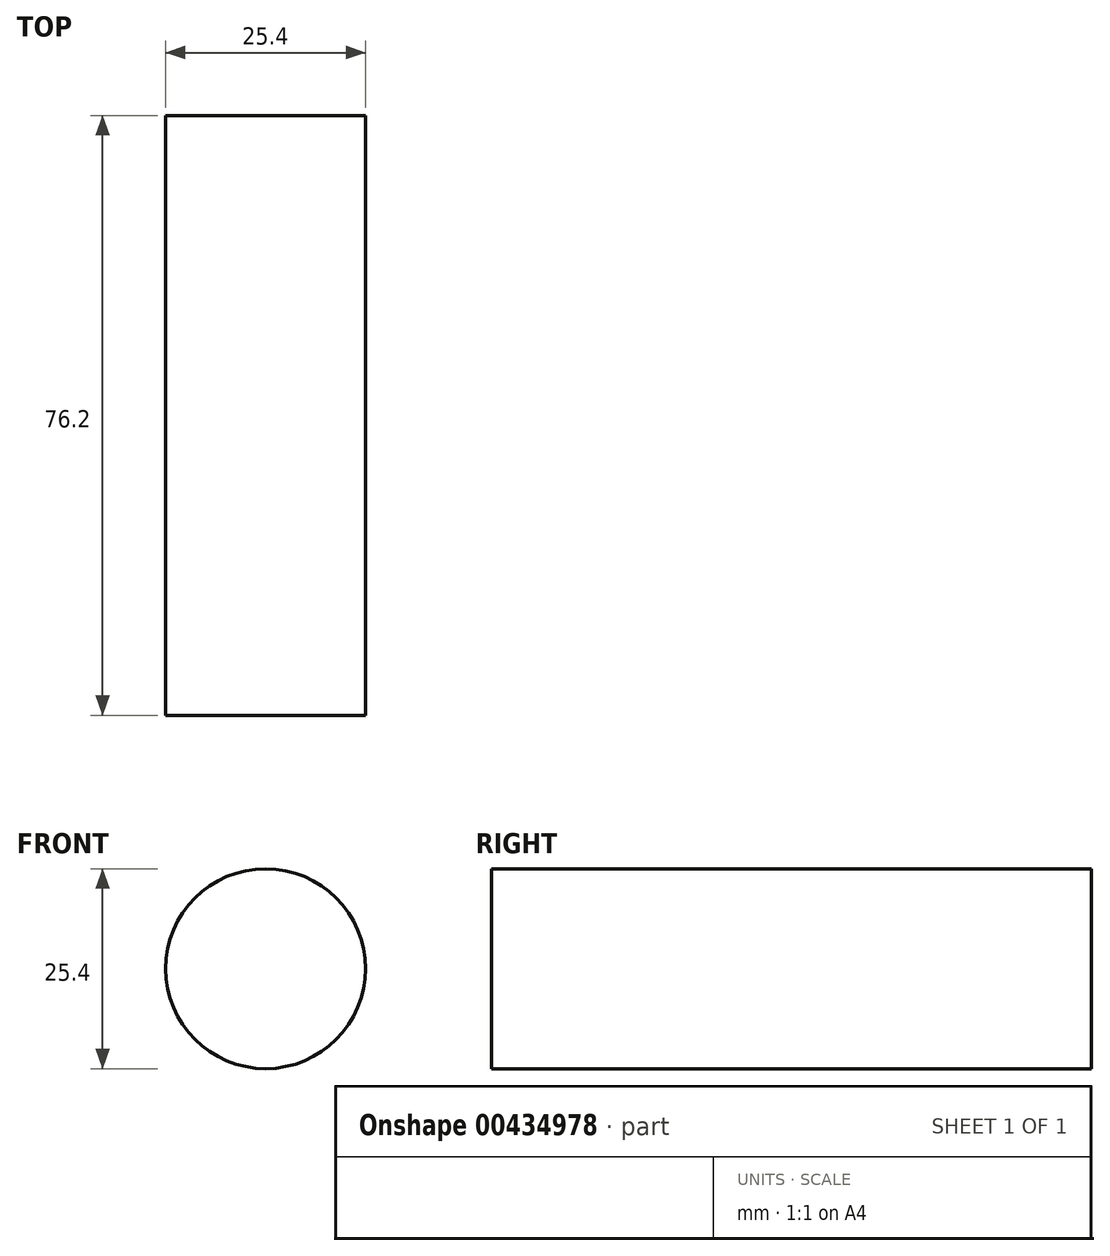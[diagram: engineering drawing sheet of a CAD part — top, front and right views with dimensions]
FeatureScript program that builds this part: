
annotation { "Feature Type Name" : "Feature", "Feature Type Description" : "" }
export const myFeature = defineFeature(function(context is Context, id is Id, definition is map)
    precondition{}
    {
        {
            var Q0;
            Q0=qCreatedBy(makeId("Front.planeOp"),FACE);
            var sketch = newSketch(context, id + "F0", { "sketchPlane" : qUnion([Q0])});
            skCircle(sketch, "E0", {"center": v(-49.46, 40.3) * mm, "radius": 12.7 * mm});
            skSolve(sketch);
        }
        {
            var Q0;
            Q0 = qSketchRegion(id + "F0", true);
            extrude(context, id + "F1", {"entities" : qUnion([Q0]), "depth" : 76.2 * mm});
        }
    });
